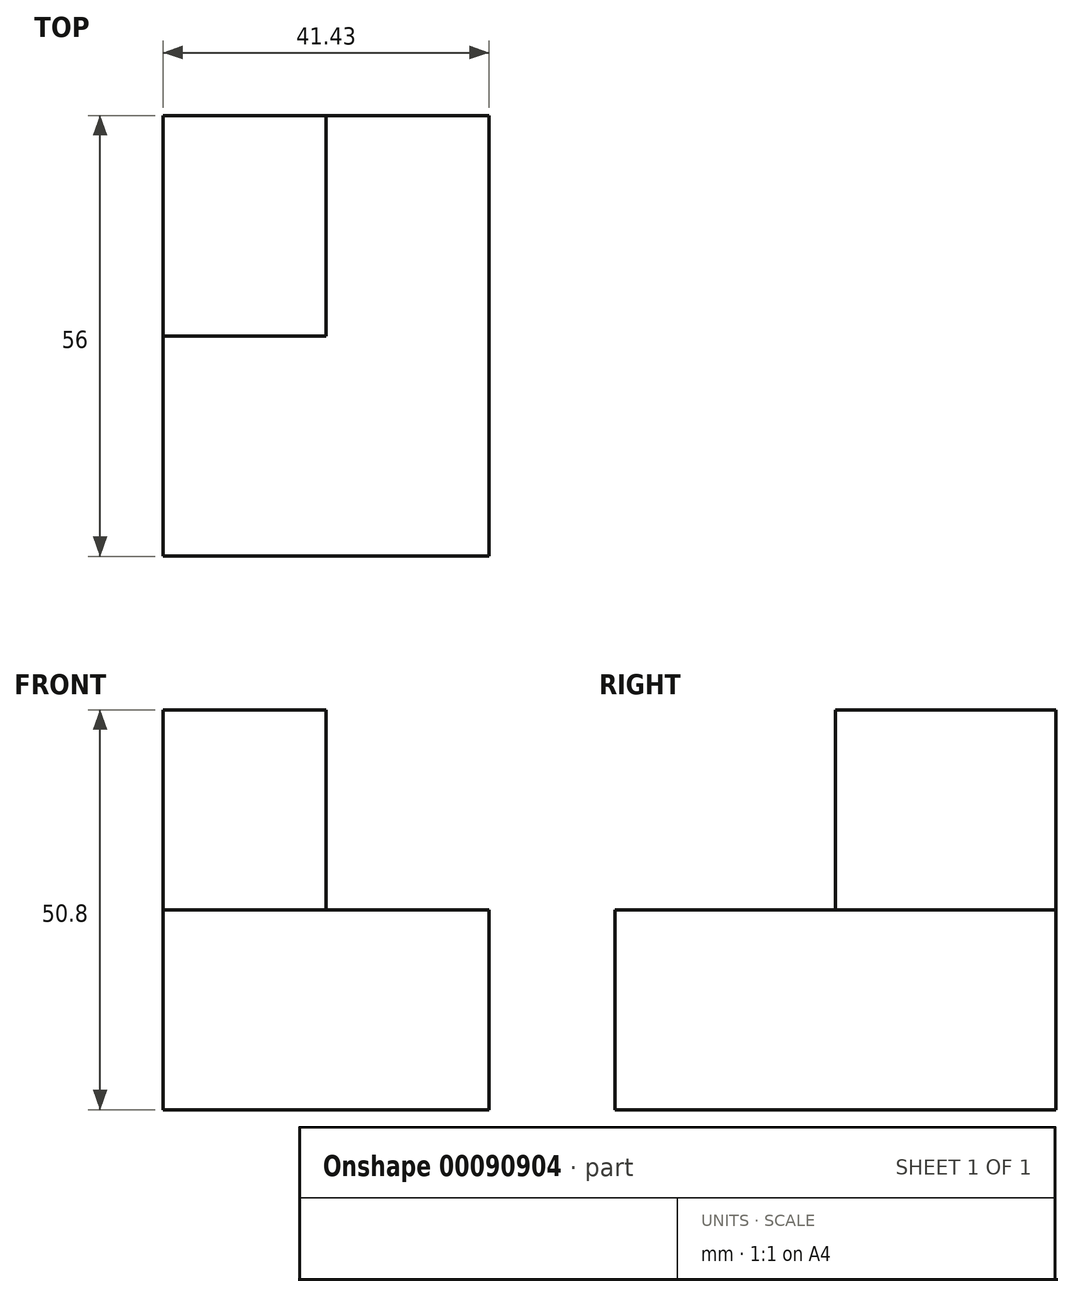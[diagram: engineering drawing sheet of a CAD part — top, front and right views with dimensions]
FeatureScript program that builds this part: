
annotation { "Feature Type Name" : "Feature", "Feature Type Description" : "" }
export const myFeature = defineFeature(function(context is Context, id is Id, definition is map)
    precondition{}
    {
        {
            var Q0;
            Q0=qCreatedBy(makeId("Top.planeOp"),FACE);
            var sketch = newSketch(context, id + "F0", { "sketchPlane" : qUnion([Q0])});
            skLineSegment(sketch, "E0", {"start": v(0, 0) * mm, "end": v(0, -56) * mm});
            skLineSegment(sketch, "E1", {"start": v(0, -56) * mm, "end": v(-41.43, -56) * mm});
            skLineSegment(sketch, "E2", {"start": v(-41.43, -56) * mm, "end": v(-41.43, 0) * mm});
            skLineSegment(sketch, "E3", {"start": v(-41.43, 0) * mm, "end": v(0, 0) * mm});
            skSolve(sketch);
        }
        {
            var Q0;
            Q0 = qSketchRegion(id + "F0", true);
            extrude(context, id + "F1", {"entities" : qUnion([Q0]), "depth" : 25.4 * mm});
        }
        {
            var Q0;
            Q0=makeQuery(id+"F1.opExtrude","CAP_FACE",FACE,{"disambiguationData":[OSD([sQuery(id+"F0.wireOp",EDGE,"E0"),sQuery(id+"F0.wireOp",EDGE,"E1"),sQuery(id+"F0.wireOp",EDGE,"E2"),sQuery(id+"F0.wireOp",EDGE,"E3")])],"isStart":false});
            var sketch = newSketch(context, id + "F2", { "sketchPlane" : qUnion([Q0])});
            skLineSegment(sketch, "E4", {"start": v(-41.43, -28) * mm, "end": v(0, -28) * mm});
            skLineSegment(sketch, "E5", {"start": v(-20.71, -28) * mm, "end": v(-20.71, 0) * mm});
            skSolve(sketch);
        }
        {
            var Q0;
            Q0 = qSketchRegion(id + "F2", true);
            var Q1;
            {var subQ3=sQuery(id+"F2.wireOp",EDGE,"E5");Q1=makeQuery(id+"F2.imprint","IMPRINT",FACE,{"disambiguationData":[TD([[makeQuery(id+"F2.imprint","IMPRINT",EDGE,{"derivedFrom":subQ3}),1.0]])]});}
            extrude(context, id + "F3", {"entities" : qUnion([Q0, Q1]), "operationType" : NewBodyOperationType.ADD, "depth" : 25.4 * mm});
        }
    });
